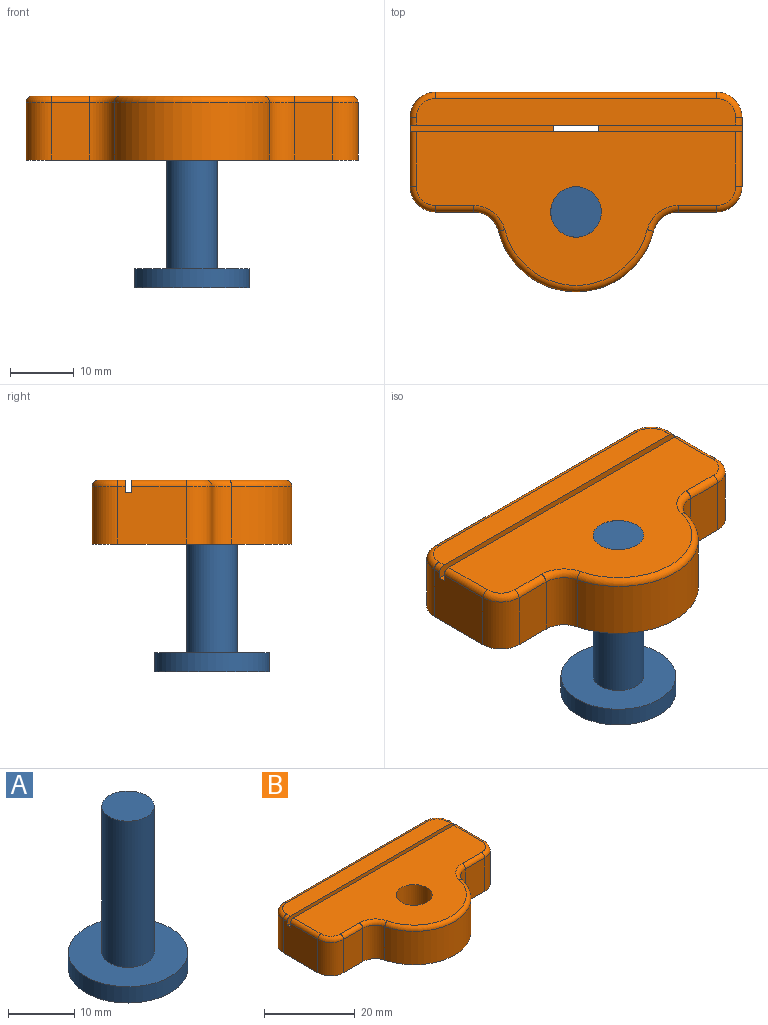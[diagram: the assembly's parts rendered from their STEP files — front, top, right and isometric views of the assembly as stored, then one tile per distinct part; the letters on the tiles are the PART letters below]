
ASSEMBLY  parts=2 mates=1
PART A: 5 faces, bbox 18x18x30 mm
  f0: cylinder r=9mm len=18mm, axis (0,0,-1), area 169.6mm2, adj f1,f2
  f1: plane 18x18mm, normal (0,0,1), area 205.5mm2, adj f0,f3
  f2: plane 18x18mm, normal (0,0,-1), area 254.5mm2, adj f0
  f3: cylinder r=3.95mm len=27mm, axis (0,0,-1), area 670.1mm2, adj f1,f4
  f4: plane 7.9x7.9mm, normal (0,0,1), area 49mm2, adj f3
PART B: 36 faces, bbox 52.6x32.6x10 mm
  f0: plane 51.96x10mm, normal (0,1,0), area 159.5mm2, adj f2,f4,f5,f11,f18,f19,f20,f28
  f1: plane 51.96x10mm, normal (0,-1,0), area 159.5mm2, adj f2,f3,f4,f5,f18,f19,f29,f33
  f2: plane 51.96x31.26mm, normal (0,0,-1), area 1154.4mm2, adj f0,f1,f4,f5,f6,f7,f8,f9
  f3: plane 49.96x4.17mm, normal (0,0,1), area 204.5mm2, adj f1,f29,f30,f31,f32,f33
  f4: plane 10.76x9mm, normal (-1,0,0), area 95.8mm2, adj f0,f1,f2,f12,f13,f28,f33,f34
  f5: plane 10.76x9mm, normal (1,0,0), area 95.8mm2, adj f0,f1,f2,f16,f17,f20,f29,f35
  f6: plane 43.96x9mm, normal (0,1,0), area 395.6mm2, adj f2,f12,f17,f31
  f7: plane 9x5.97mm, normal (0,-1,0), area 53.7mm2, adj f2,f13,f14,f26
  f8: cylinder r=12.5mm len=24.25mm, axis (0,0,-1), area 298.3mm2, adj f2,f14,f15,f24
  f9: plane 9x5.97mm, normal (0,-1,0), area 53.7mm2, adj f2,f15,f16,f22
  f10: cylinder r=3.96mm len=10mm, axis (0,0,-1), area 248.8mm2, adj f2,f11
  f11: plane 49.96x24.09mm, normal (0,0,1), area 763.9mm2, adj f0,f10,f20,f21,f22,f23,f24,f25
  f12: cylinder r=4mm len=9mm, axis (0,0,1), area 56.5mm2, adj f2,f4,f6,f32
  f13: cylinder r=4mm len=9mm, axis (0,0,-1), area 56.5mm2, adj f2,f4,f7,f27
  f14: cylinder r=4mm len=9mm, axis (0,0,-1), area 47.7mm2, adj f2,f7,f8,f25
  f15: cylinder r=4mm len=9mm, axis (0,0,-1), area 47.7mm2, adj f2,f8,f9,f23
  f16: cylinder r=4mm len=9mm, axis (0,0,-1), area 56.5mm2, adj f2,f5,f9,f21
  f17: cylinder r=4mm len=9mm, axis (0,0,-1), area 56.5mm2, adj f2,f5,f6,f30
  f18: plane 8x1mm, normal (1,0,0), area 8mm2, adj f0,f1,f2,f34
  f19: plane 8x1mm, normal (-1,0,0), area 8mm2, adj f0,f1,f2,f35
  f20: cylinder r=1mm len=8.59mm, axis (0,-1,0), area 13.5mm2, adj f0,f5,f11,f21
  f21: torus R=3mm, axis (0,0,1), area 9mm2, adj f11,f16,f20,f22
  f22: cylinder r=1mm len=5.97mm, axis (-1,0,0), area 9.4mm2, adj f9,f11,f21,f23
  f23: torus R=5mm, axis (0,0,1), area 9.1mm2, adj f11,f15,f22,f24
  f24: torus R=11.5mm, axis (0,0,1), area 50.6mm2, adj f8,f11,f23,f25
  f25: torus R=5mm, axis (0,0,1), area 9.1mm2, adj f11,f14,f24,f26
  f26: cylinder r=1mm len=5.97mm, axis (-1,0,0), area 9.4mm2, adj f7,f11,f25,f27
  f27: torus R=3mm, axis (0,0,1), area 9mm2, adj f11,f13,f26,f28
  f28: cylinder r=1mm len=8.59mm, axis (0,1,0), area 13.5mm2, adj f0,f4,f11,f27
  f29: cylinder r=1mm len=1.17mm, axis (0,-1,0), area 1.8mm2, adj f1,f3,f5,f30
  f30: torus R=3mm, axis (0,0,1), area 9mm2, adj f3,f17,f29,f31
  f31: cylinder r=1mm len=43.96mm, axis (1,0,0), area 69mm2, adj f3,f6,f30,f32
  f32: torus R=3mm, axis (0,0,1), area 9mm2, adj f3,f12,f31,f33
  f33: cylinder r=1mm len=1.17mm, axis (0,1,0), area 1.8mm2, adj f1,f3,f4,f32
  f34: plane 22.48x1mm, normal (0,0,1), area 22.5mm2, adj f0,f1,f4,f18
  f35: plane 22.48x1mm, normal (0,0,1), area 22.5mm2, adj f0,f1,f5,f19
PLACE A t=(-18.47,-11.68,-16.52)mm
PLACE B t=(-18.47,-11.68,3.48)mm
MATE revolute B.f10 <-> A.f3  axis (0,0,1) through (-18.47,-11.68,13.48)mm
